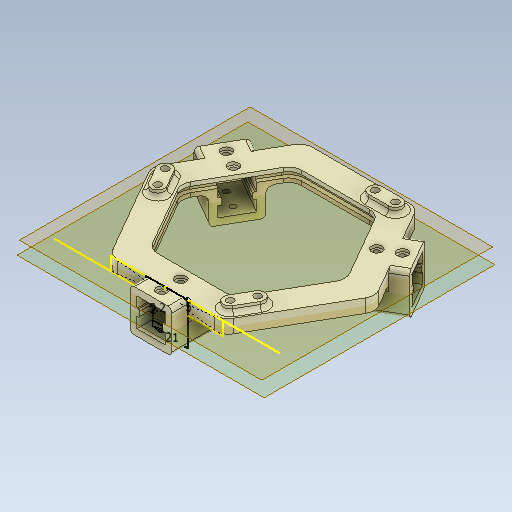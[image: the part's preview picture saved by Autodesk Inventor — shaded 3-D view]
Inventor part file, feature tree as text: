
AUTODESK INVENTOR PART (.ipt)
format: ipt  version: 2021 (Build 250183000, 183)  size: 600,064 bytes
history: native  units: mm
features: extrude x10, other x6, sketch x6, fillet x2, projected_geometry x2, mirror x1, pattern_circular x1, reference x1
ambient origin geometry x8: Origin, YZ Plane, XZ Plane, XY Plane, X Axis, Y Axis, Z Axis, Center Point
bodies: Body1 (feature_tree)
feature tree (29):
  other  "솔리드1"
  sketch  "스케치1"
  extrude  "돌출1"  Depth=12.7mm
  sketch  "스케치2"
  extrude  "돌출2"  Depth=80.0mm
  extrude  "돌출3"  Depth=5.3mm
  fillet  "모깎기1"  Radius=5.0mm
  extrude  "돌출11"  Depth=20.0mm
  sketch  "스케치15"
  extrude  "돌출18"  Depth=5.0mm
  extrude  "돌출19"  Depth=20.0mm
  extrude  "돌출20"  Depth=5.0mm
  sketch  "스케치20"
  extrude  "돌출25"  Depth=20.0mm
  extrude  "돌출26"  Depth=10.0mm TaperAngle=0.0deg
  other  "작업 평면15"
  mirror  "미러6"
  pattern_circular  "원형 패턴6"  [2 undecoded]
  fillet  "모깎기5"  Radius=5.0mm
  other  "작업 평면16"
  extrude  "돌출27"  TaperAngle=0.0deg  [1 undecoded]
  sketch  "스케치9"
  projected_geometry  "투영된 루프10"
  projected_geometry  "투영된 루프12"
  sketch  "스케치21"
  reference  "참조1"
  other  "<userpath>\Desktop\개별연구\힘-토크 측정기기_v2\힘-토크 측정기기_v2.iam"
  other  "힘-토크 측정기기_v2.iam"
  other  "connector_v2:1"
note: 3 required parameter values undecoded (feature->parameter linkage not recoverable at this tier; creation-order binding heuristic only, values carry confidence <= 0.55)
